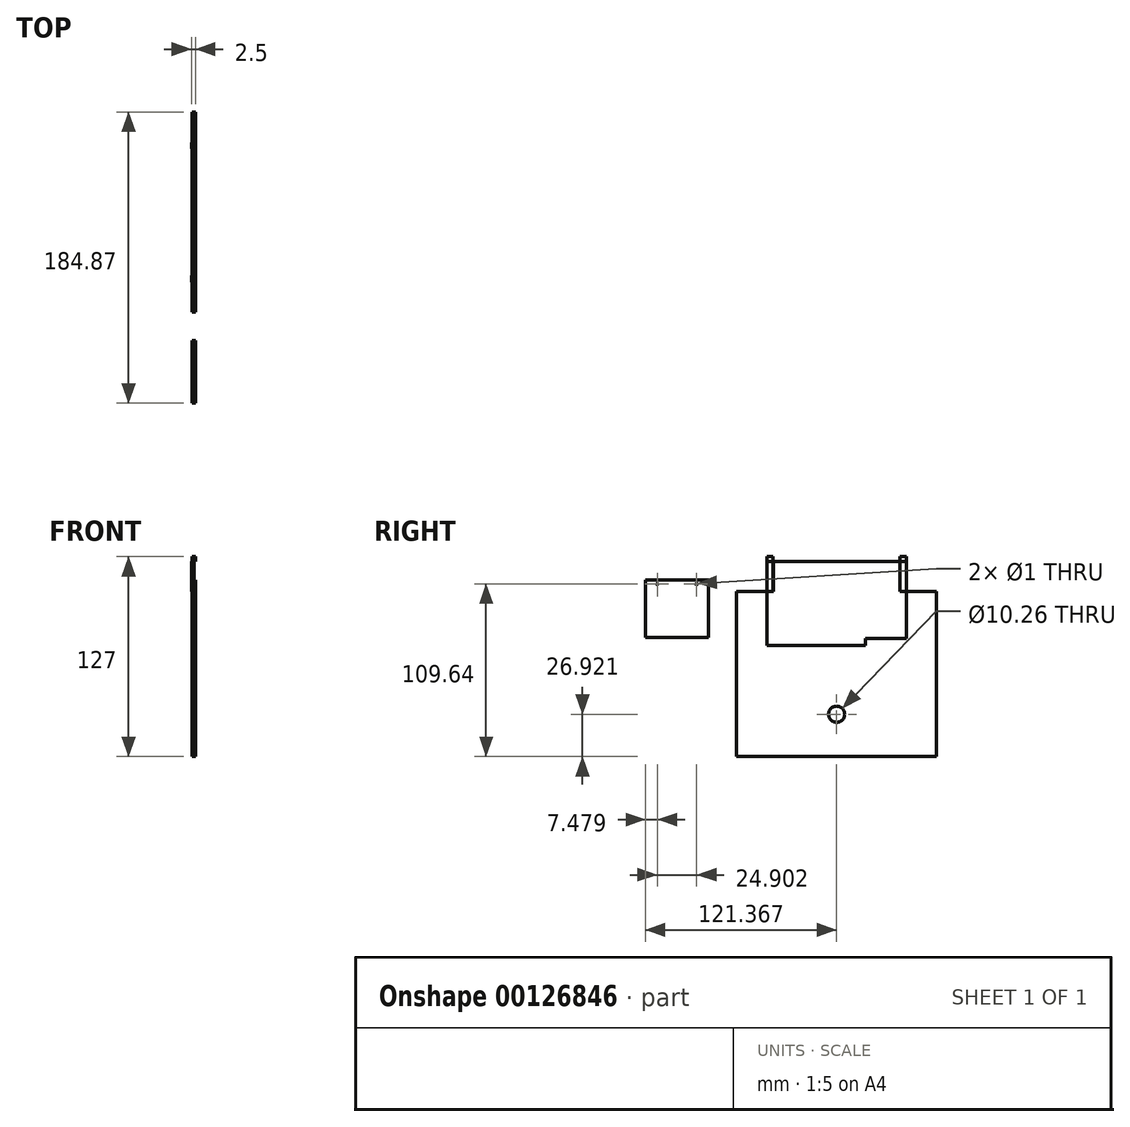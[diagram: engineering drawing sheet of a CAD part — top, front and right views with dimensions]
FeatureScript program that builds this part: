
annotation { "Feature Type Name" : "Feature", "Feature Type Description" : "" }
export const myFeature = defineFeature(function(context is Context, id is Id, definition is map)
    precondition{}
    {
        {
            var Q0;
            Q0=qCreatedBy(makeId("Right.planeOp"),FACE);
            var sketch = newSketch(context, id + "F0", { "sketchPlane" : qUnion([Q0])});
            skLineSegment(sketch, "E0.bottom", {"start": v(-47.44, 80.54) * mm, "end": v(79.56, 80.54) * mm});
            skLineSegment(sketch, "E0.top", {"start": v(-47.44, -46.46) * mm, "end": v(79.56, -46.46) * mm});
            skLineSegment(sketch, "E0.left", {"start": v(-47.44, 80.54) * mm, "end": v(-47.44, -46.46) * mm});
            skLineSegment(sketch, "E0.right", {"start": v(79.56, 80.54) * mm, "end": v(79.56, -46.46) * mm});
            skLineSegment(sketch, "E1.bottom", {"start": v(-28.24, 77.54) * mm, "end": v(34.36, 77.54) * mm});
            skLineSegment(sketch, "E1.top", {"start": v(-28.24, 24.14) * mm, "end": v(34.36, 24.14) * mm});
            skLineSegment(sketch, "E1.left", {"start": v(-28.24, 77.54) * mm, "end": v(-28.24, 24.14) * mm});
            skLineSegment(sketch, "E1.right", {"start": v(34.36, 77.54) * mm, "end": v(34.36, 24.14) * mm});
            skLineSegment(sketch, "E2.bottom", {"start": v(34.36, 77.54) * mm, "end": v(60.36, 77.54) * mm});
            skLineSegment(sketch, "E2.top", {"start": v(34.36, 28.74) * mm, "end": v(60.36, 28.74) * mm});
            skLineSegment(sketch, "E2.left", {"start": v(34.36, 77.54) * mm, "end": v(34.36, 28.74) * mm});
            skLineSegment(sketch, "E2.right", {"start": v(60.36, 77.54) * mm, "end": v(60.36, 28.74) * mm});
            skLineSegment(sketch, "E3.bottom", {"start": v(34.36, 77.54) * mm, "end": v(34.36, 77.54) * mm});
            skLineSegment(sketch, "E3.top", {"start": v(34.36, 28.74) * mm, "end": v(34.36, 28.74) * mm});
            skLineSegment(sketch, "E4.bottom", {"start": v(-24.24, 80.54) * mm, "end": v(-47.44, 80.54) * mm});
            skLineSegment(sketch, "E4.top", {"start": v(-24.24, 58.54) * mm, "end": v(-47.44, 58.54) * mm});
            skLineSegment(sketch, "E4.left", {"start": v(-24.24, 80.54) * mm, "end": v(-24.24, 58.54) * mm});
            skLineSegment(sketch, "E4.right", {"start": v(-47.44, 80.54) * mm, "end": v(-47.44, 58.54) * mm});
            skLineSegment(sketch, "E5.bottom", {"start": v(79.56, 80.54) * mm, "end": v(56.36, 80.54) * mm});
            skLineSegment(sketch, "E5.top", {"start": v(79.56, 58.54) * mm, "end": v(56.36, 58.54) * mm});
            skLineSegment(sketch, "E5.left", {"start": v(79.56, 80.54) * mm, "end": v(79.56, 58.54) * mm});
            skLineSegment(sketch, "E5.right", {"start": v(56.36, 80.54) * mm, "end": v(56.36, 58.54) * mm});
            skLineSegment(sketch, "E6.bottom", {"start": v(-47.44, 80.54) * mm, "end": v(-28.24, 80.54) * mm});
            skLineSegment(sketch, "E6.top", {"start": v(-47.44, 58.54) * mm, "end": v(-28.24, 58.54) * mm});
            skLineSegment(sketch, "E6.right", {"start": v(-28.24, 80.54) * mm, "end": v(-28.24, 58.54) * mm});
            skLineSegment(sketch, "E7.bottom", {"start": v(79.56, 80.54) * mm, "end": v(60.36, 80.54) * mm});
            skLineSegment(sketch, "E7.top", {"start": v(79.56, 58.54) * mm, "end": v(60.36, 58.54) * mm});
            skLineSegment(sketch, "E7.right", {"start": v(60.36, 80.54) * mm, "end": v(60.36, 58.54) * mm});
            skPoint(sketch, "E8", {"position": v(-37.84, 80.54) * mm});
            skCircle(sketch, "E9", {"center": v(-38.38, 80.42) * mm, "radius": 0 * mm});
            skCircle(sketch, "E10", {"center": v(-37.38, 80.42) * mm, "radius": 0 * mm});
            skPoint(sketch, "E11", {"position": v(69.96, 80.54) * mm});
            skCircle(sketch, "E12", {"center": v(70.43, 80.44) * mm, "radius": 0 * mm});
            skCircle(sketch, "E13", {"center": v(69.43, 80.44) * mm, "radius": 0 * mm});
            skPoint(sketch, "E14", {"position": v(16.06, 80.54) * mm});
            skCircle(sketch, "E15", {"center": v(16.06, -19.54) * mm, "radius": 5.13 * mm});
            skSolve(sketch);
        }
        {
            var Q0;
            Q0=qCreatedBy(makeId("Right.planeOp"),FACE);
            var sketch = newSketch(context, id + "F1", { "sketchPlane" : qUnion([Q0])});
            skLineSegment(sketch, "E16.bottom", {"start": v(-105.31, 29.36) * mm, "end": v(-65.44, 29.36) * mm});
            skLineSegment(sketch, "E16.top", {"start": v(-105.31, 65.68) * mm, "end": v(-65.44, 65.68) * mm});
            skLineSegment(sketch, "E16.left", {"start": v(-105.31, 65.68) * mm, "end": v(-105.31, 29.36) * mm});
            skLineSegment(sketch, "E16.right", {"start": v(-65.44, 65.68) * mm, "end": v(-65.44, 29.36) * mm});
            skCircle(sketch, "E17", {"center": v(-97.83, 63.18) * mm, "radius": 0.5 * mm});
            skCircle(sketch, "E18", {"center": v(-72.93, 63.18) * mm, "radius": 0.5 * mm});
            skSolve(sketch);
        }
        {
            var Q0;
            Q0=makeQuery(id+"F1.imprint","IMPRINT",FACE,{"disambiguationData":[TD([[makeQuery(id+"F1.imprint","IMPRINT",EDGE,{"derivedFrom":sQuery(id+"F1.wireOp",EDGE,"E16.bottom")}),1.0]])]});
            extrude(context, id + "F2", {"entities" : qUnion([Q0]), "depth" : 2 * mm});
        }
        {
            var Q0;
            Q0=sQuery(id+"F0.wireOp",EDGE,"E2.left");
            extrude(context, id + "F3", {"bodyType" : ToolBodyType.SURFACE, "surfaceEntities" : qUnion([Q0]), "depth" : 1 * mm});
        }
        {
            var Q0;
            {var subQ1=sQuery(id+"F0.wireOp",EDGE,"E1.top");Q0=makeQuery(id+"F0.imprint","IMPRINT",FACE,{"disambiguationData":[TD([[makeQuery(id+"F0.imprint","IMPRINT",EDGE,{"derivedFrom":subQ1}),1.0]])]});}
            var Q1;
            {var subQ2=sQuery(id+"F0.wireOp",EDGE,"E2.top");Q1=makeQuery(id+"F0.imprint","IMPRINT",FACE,{"disambiguationData":[TD([[makeQuery(id+"F0.imprint","IMPRINT",EDGE,{"derivedFrom":subQ2}),1.0]])]});}
            extrude(context, id + "F4", {"entities" : qUnion([Q0, Q1]), "depth" : 0.5 * mm});
        }
        {
            var Q0;
            Q0=makeQuery(id+"F4.opExtrude","CAP_FACE",FACE,{"disambiguationData":[OSD([sQuery(id+"F0.wireOp",EDGE,"E1.bottom"),sQuery(id+"F0.wireOp",EDGE,"E1.top"),sQuery(id+"F0.wireOp",EDGE,"E1.left"),sQuery(id+"F0.wireOp",EDGE,"E1.right"),sQuery(id+"F0.wireOp",EDGE,"E2.bottom"),sQuery(id+"F0.wireOp",EDGE,"E2.top"),sQuery(id+"F0.wireOp",EDGE,"E2.right")])],"isStart":false});
            shell(context, id + "F5", {"entities" : qUnion([Q0]), "thickness" : 0.01 * mm});
        }
        {
            var Q0;
            Q0=makeQuery(id+"F0.imprint","IMPRINT",FACE,{"disambiguationData":[TD([[makeQuery(id+"F0.imprint","IMPRINT",EDGE,{"derivedFrom":sQuery(id+"F0.wireOp",EDGE,"E0.top")}),1.0]])]});
            extrude(context, id + "F6", {"entities" : qUnion([Q0]), "depth" : 2 * mm});
        }
        {
            var Q0;
            {var subQ2=sQuery(id+"F0.wireOp",EDGE,"E6.bottom");Q0=makeQuery(id+"F0.imprint","IMPRINT",FACE,{"disambiguationData":[TD([[makeQuery(id+"F0.imprint","IMPRINT",EDGE,{"derivedFrom":subQ2}),-1.0]])]});}
            var Q1;
            {var subQ2=sQuery(id+"F0.wireOp",EDGE,"E7.bottom");Q1=makeQuery(id+"F0.imprint","IMPRINT",FACE,{"disambiguationData":[TD([[makeQuery(id+"F0.imprint","IMPRINT",EDGE,{"derivedFrom":subQ2}),1.0]])]});}
            var Q2;
            {var subQ7=sQuery(id+"F0.wireOp",EDGE,"E0.bottom");Q2=makeQuery(id+"F0.imprint","IMPRINT",FACE,{"disambiguationData":[TD([[makeQuery(id+"F0.imprint","IMPRINT",EDGE,{"derivedFrom":subQ7}),-1.0]])]});}
            extrude(context, id + "F7", {"entities" : qUnion([Q0, Q1, Q2]), "depth" : 2 * mm});
        }
        {
            var Q0;
            {var subQ5=sQuery(id+"F0.wireOp",EDGE,"E4.bottom");Q0=makeQuery(id+"F0.imprint","IMPRINT",FACE,{"disambiguationData":[TD([[makeQuery(id+"F0.imprint","IMPRINT",EDGE,{"derivedFrom":subQ5}),1.0]])]});}
            var Q1;
            {var subQ5=sQuery(id+"F0.wireOp",EDGE,"E4.top");Q1=makeQuery(id+"F0.imprint","IMPRINT",FACE,{"disambiguationData":[TD([[makeQuery(id+"F0.imprint","IMPRINT",EDGE,{"derivedFrom":subQ5}),-1.0]])]});}
            var Q2;
            {var subQ5=sQuery(id+"F0.wireOp",EDGE,"E5.top");Q2=makeQuery(id+"F0.imprint","IMPRINT",FACE,{"disambiguationData":[TD([[makeQuery(id+"F0.imprint","IMPRINT",EDGE,{"derivedFrom":subQ5}),-1.0]])]});}
            var Q3;
            {var subQ5=sQuery(id+"F0.wireOp",EDGE,"E5.bottom");Q3=makeQuery(id+"F0.imprint","IMPRINT",FACE,{"disambiguationData":[TD([[makeQuery(id+"F0.imprint","IMPRINT",EDGE,{"derivedFrom":subQ5}),1.0]])]});}
            extrude(context, id + "F8", {"entities" : qUnion([Q0, Q1, Q2, Q3]), "depth" : 1 * mm, "hasSecondDirection" : true, "secondDirectionOppositeDirection" : true, "secondDirectionDepth" : 0.5 * mm});
        }
    });
